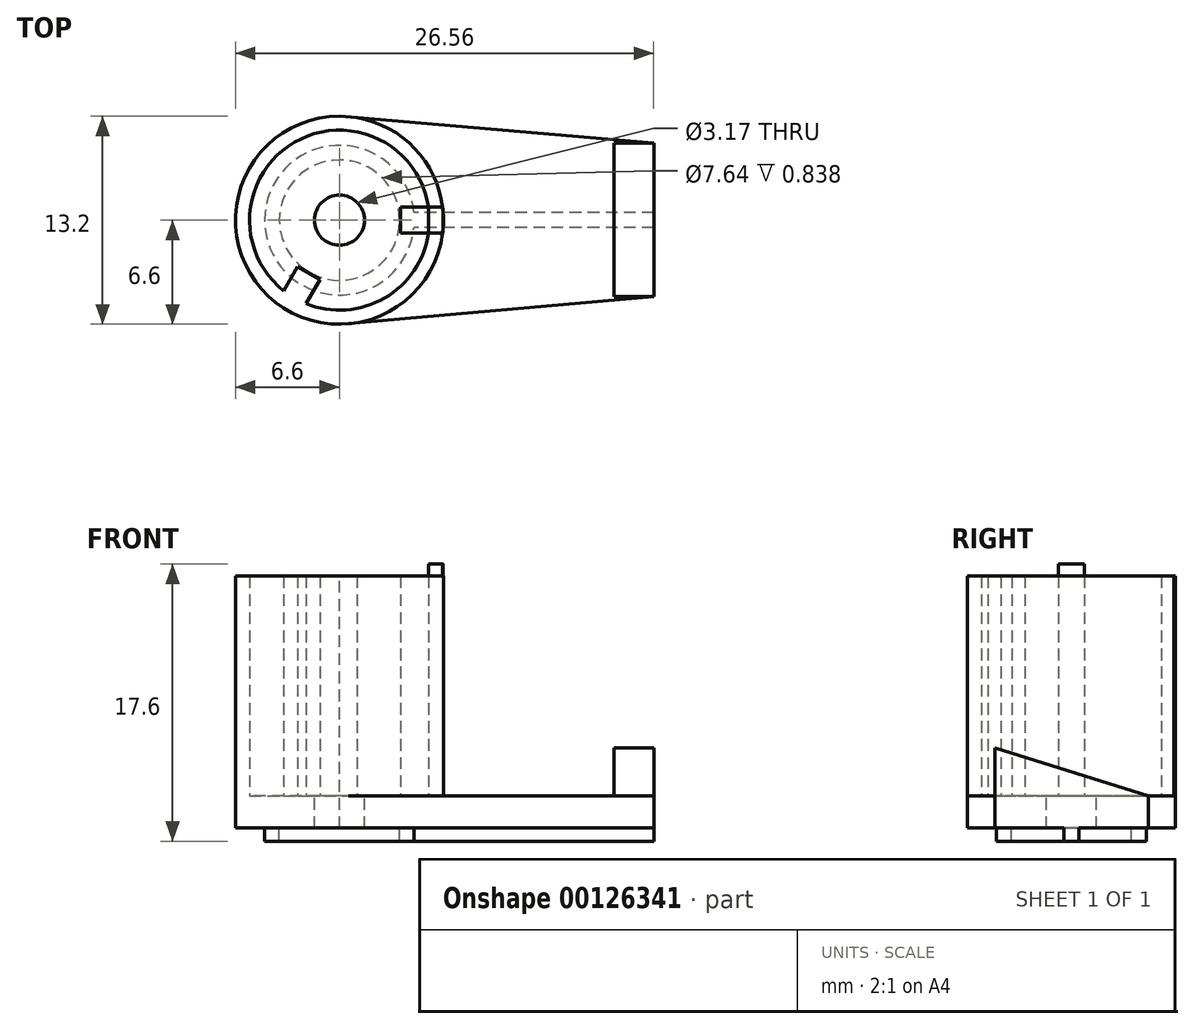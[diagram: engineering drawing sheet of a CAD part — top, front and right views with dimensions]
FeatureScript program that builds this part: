
annotation { "Feature Type Name" : "Feature", "Feature Type Description" : "" }
export const myFeature = defineFeature(function(context is Context, id is Id, definition is map)
    precondition{}
    {
        {
            var Q0;
            Q0=qCreatedBy(makeId("Top.planeOp"),FACE);
            var sketch = newSketch(context, id + "F0", { "sketchPlane" : qUnion([Q0])});
            skCircle(sketch, "E0", {"center": v(0, 0) * mm, "radius": 6.6 * mm});
            skCircle(sketch, "E1.0", {"center": v(0, 0) * mm, "radius": 5.72 * mm});
            skLineSegment(sketch, "E2.right", {"start": v(19.96, 4.9) * mm, "end": v(19.96, -4.85) * mm});
            skLineSegment(sketch, "E3.trimOffspring", {"start": v(0, -6.6) * mm, "end": v(0, -6.7) * mm});
            skLineSegment(sketch, "E4.trimOffspring", {"start": v(0, -6.6) * mm, "end": v(0, -6.63) * mm});
            skLineSegment(sketch, "E5", {"start": v(0, 6.6) * mm, "end": v(19.96, 4.9) * mm});
            skLineSegment(sketch, "E6", {"start": v(0, -6.63) * mm, "end": v(19.96, -4.85) * mm});
            skPoint(sketch, "E7.orphan", {"position": v(19.96, 6.67) * mm});
            skPoint(sketch, "E2.top.end.orphan", {"position": v(19.96, -6.63) * mm});
            skPoint(sketch, "E8.top.end.orphan", {"position": v(-6.7, -6.63) * mm});
            skCircle(sketch, "E9", {"center": v(0, 0) * mm, "radius": 1.59 * mm});
            skSolve(sketch);
        }
        {
            var Q0;
            {var subQ0=sQuery(id+"F0.wireOp",EDGE,"E5");var subQ1=sQuery(id+"F0.wireOp",EDGE,"E0");var subQ2=makeQuery(id+"F0.imprint","INTERSECT",VERTEX,{"disambiguationData":[OD(0.0)],"derivedFrom":[subQ1,subQ0]});Q0=makeQuery(id+"F0.imprint","IMPRINT",FACE,{"disambiguationData":[TD([[makeQuery(id+"F0.imprint","IMPRINT",EDGE,{"disambiguationData":[TD([[subQ2,1.0]])],"derivedFrom":subQ1}),1.0]])]});}
            var Q1;
            {var subQ0=sQuery(id+"F0.wireOp",EDGE,"E4.trimOffspring");Q1=makeQuery(id+"F0.imprint","IMPRINT",FACE,{"disambiguationData":[TD([[makeQuery(id+"F0.imprint","IMPRINT",EDGE,{"derivedFrom":subQ0}),1.0]])]});}
            var Q2;
            Q2=makeQuery(id+"F0.imprint","IMPRINT",FACE,{"disambiguationData":[TD([[makeQuery(id+"F0.imprint","IMPRINT",EDGE,{"derivedFrom":sQuery(id+"F0.wireOp",EDGE,"E1.0")}),-1.0]])]});
            var Q3;
            {var subQ5=sQuery(id+"F0.wireOp",EDGE,"E2.right");Q3=makeQuery(id+"F0.imprint","IMPRINT",FACE,{"disambiguationData":[TD([[makeQuery(id+"F0.imprint","IMPRINT",EDGE,{"derivedFrom":subQ5}),-1.0]])]});}
            var Q4;
            Q4=makeQuery(id+"F0.imprint","IMPRINT",FACE,{"disambiguationData":[TD([[makeQuery(id+"F0.imprint","IMPRINT",EDGE,{"derivedFrom":sQuery(id+"F0.wireOp",EDGE,"E1.0")}),1.0]])]});
            extrude(context, id + "F1", {"entities" : qUnion([Q0, Q1, Q2, Q3, Q4]), "oppositeDirection" : true, "depth" : 2.03 * mm});
        }
        {
            var Q0;
            Q0=makeQuery(id+"F0.imprint","IMPRINT",FACE,{"disambiguationData":[TD([[makeQuery(id+"F0.imprint","IMPRINT",EDGE,{"derivedFrom":sQuery(id+"F0.wireOp",EDGE,"E1.0")}),-1.0]])]});
            extrude(context, id + "F2", {"entities" : qUnion([Q0]), "operationType" : NewBodyOperationType.ADD, "depth" : 13.97 * mm});
        }
        {
            var Q0;
            Q0=makeQuery(id+"F1.opExtrude","SWEPT_FACE",FACE,{"disambiguationData":[OSD([sQuery(id+"F0.wireOp",EDGE,"E2.right")])]});
            var sketch = newSketch(context, id + "F3", { "sketchPlane" : qUnion([Q0])});
            skLineSegment(sketch, "E10", {"start": v(4.9, 0) * mm, "end": v(-4.85, 3.05) * mm});
            skLineSegment(sketch, "E11", {"start": v(-4.85, 3.05) * mm, "end": v(-4.85, 0) * mm});
            skSolve(sketch);
        }
        {
            var Q0;
            Q0 = qSketchRegion(id + "F3", true);
            var Q1;
            Q1=makeQuery(id+"F3.imprint","IMPRINT",FACE,{"disambiguationData":[TD([[makeQuery(id+"F3.imprint","IMPRINT",EDGE,{"derivedFrom":sQuery(id+"F3.wireOp",EDGE,"E10")}),1.0]])]});
            extrude(context, id + "F4", {"entities" : qUnion([Q0, Q1]), "operationType" : NewBodyOperationType.ADD, "oppositeDirection" : true, "depth" : 2.54 * mm});
        }
        {
            var Q0;
            Q0=makeQuery(id+"F0.imprint","IMPRINT",FACE,{"disambiguationData":[TD([[makeQuery(id+"F0.imprint","IMPRINT",EDGE,{"derivedFrom":sQuery(id+"F0.wireOp",EDGE,"E1.0")}),1.0]])]});
            var sketch = newSketch(context, id + "F5", { "sketchPlane" : qUnion([Q0])});
            skLineSegment(sketch, "E12", {"start": v(0, 0) * mm, "end": v(20.41, 0) * mm, "construction": true});
            skLineSegment(sketch, "E13", {"start": v(20.41, 0) * mm, "end": v(5.65, 0) * mm, "construction": true});
            skLineSegment(sketch, "E14.bottom", {"start": v(6.44, -0.82) * mm, "end": v(3.88, -0.82) * mm});
            skLineSegment(sketch, "E14.top", {"start": v(6.44, 0.82) * mm, "end": v(3.88, 0.82) * mm});
            skLineSegment(sketch, "E14.left", {"start": v(6.44, -0.82) * mm, "end": v(6.44, 0.82) * mm});
            skLineSegment(sketch, "E14.right", {"start": v(3.88, -0.82) * mm, "end": v(3.88, 0.82) * mm});
            skPoint(sketch, "E14.middle", {"position": v(5.16, 0) * mm});
            skPoint(sketch, "E15.center", {"position": v(0, 0) * mm});
            skLineSegment(sketch, "E16.1.0", {"start": v(-2.51, -5.98) * mm, "end": v(-1.23, -3.77) * mm});
            skLineSegment(sketch, "E16.1.1", {"start": v(-3.93, -5.17) * mm, "end": v(-2.65, -2.95) * mm});
            skLineSegment(sketch, "E16.1.2", {"start": v(-3.93, -5.17) * mm, "end": v(-2.51, -5.98) * mm});
            skLineSegment(sketch, "E16.1.3", {"start": v(-2.65, -2.95) * mm, "end": v(-1.23, -3.77) * mm});
            skLineSegment(sketch, "E16.anchor1", {"start": v(0, 0) * mm, "end": v(3.88, -0.82) * mm, "construction": true});
            skLineSegment(sketch, "E16.anchor2", {"start": v(0, 0) * mm, "end": v(-2.65, -2.95) * mm, "construction": true});
            skSolve(sketch);
        }
        {
            var Q0;
            Q0 = qSketchRegion(id + "F5", true);
            extrude(context, id + "F6", {"entities" : qUnion([Q0]), "operationType" : NewBodyOperationType.ADD, "depth" : 13.97 * mm});
        }
        {
            var Q0;
            Q0=makeQuery(id+"F1.opExtrude","CAP_FACE",FACE,{"disambiguationData":[OSD([sQuery(id+"F0.wireOp",EDGE,"E0"),sQuery(id+"F0.wireOp",EDGE,"E2.right"),sQuery(id+"F0.wireOp",EDGE,"E4.trimOffspring"),sQuery(id+"F0.wireOp",EDGE,"E5"),sQuery(id+"F0.wireOp",EDGE,"E6"),sQuery(id+"F0.wireOp",EDGE,"E9")])],"isStart":false});
            var sketch = newSketch(context, id + "F7", { "sketchPlane" : qUnion([Q0])});
            skLineSegment(sketch, "E17", {"start": v(0, 0) * mm, "end": v(3.82, 0) * mm, "construction": true});
            skCircle(sketch, "E18", {"center": v(0, 0) * mm, "radius": 3.82 * mm});
            skArc(sketch, "E19.0", {"start": v(4.73, 0.47) * mm, "mid": v(-4.75, 0) * mm, "end": v(4.73, -0.47) * mm});
            skLineSegment(sketch, "E20.bottom", {"start": v(19.96, -0.47) * mm, "end": v(4.73, -0.47) * mm});
            skLineSegment(sketch, "E20.top", {"start": v(19.96, 0.47) * mm, "end": v(4.73, 0.47) * mm});
            skLineSegment(sketch, "E20.left", {"start": v(19.96, -0.47) * mm, "end": v(19.96, 0.47) * mm});
            skPoint(sketch, "E20.middle", {"position": v(11.17, 0) * mm});
            skLineSegment(sketch, "E21.trimOffspring", {"start": v(4.75, 0) * mm, "end": v(19.96, 0) * mm, "construction": true});
            skSolve(sketch);
        }
        {
            var Q0;
            Q0=makeQuery(id+"F7.imprint","IMPRINT",FACE,{"disambiguationData":[TD([[makeQuery(id+"F7.imprint","IMPRINT",EDGE,{"derivedFrom":sQuery(id+"F7.wireOp",EDGE,"E18")}),-1.0]])]});
            extrude(context, id + "F8", {"entities" : qUnion([Q0]), "operationType" : NewBodyOperationType.ADD, "depth" : 0.84 * mm});
        }
        {
            var Q0;
            Q0=makeQuery(id+"F6.boolean.opBoolean","MERGE",FACE,{"derivedFrom":[makeQuery(id+"F2.opExtrude","CAP_FACE",FACE,{"disambiguationData":[OSD([sQuery(id+"F0.wireOp",EDGE,"E0"),sQuery(id+"F0.wireOp",EDGE,"E1.0"),sQuery(id+"F0.wireOp",EDGE,"E5")])],"isStart":false}),makeQuery(id+"F6.opExtrude","CAP_FACE",FACE,{"disambiguationData":[OSD([sQuery(id+"F5.wireOp",EDGE,"E14.bottom"),sQuery(id+"F5.wireOp",EDGE,"E14.top"),sQuery(id+"F5.wireOp",EDGE,"E14.left"),sQuery(id+"F5.wireOp",EDGE,"E14.right")])],"isStart":false}),makeQuery(id+"F6.opExtrude","CAP_FACE",FACE,{"disambiguationData":[OSD([sQuery(id+"F5.wireOp",EDGE,"E16.1.0"),sQuery(id+"F5.wireOp",EDGE,"E16.1.1"),sQuery(id+"F5.wireOp",EDGE,"E16.1.2"),sQuery(id+"F5.wireOp",EDGE,"E16.1.3")])],"isStart":false})]});
            var sketch = newSketch(context, id + "F9", { "sketchPlane" : qUnion([Q0])});
            skLineSegment(sketch, "E22.bottom", {"start": v(5.66, 0.82) * mm, "end": v(6.55, 0.82) * mm});
            skLineSegment(sketch, "E22.top", {"start": v(5.66, -0.82) * mm, "end": v(6.55, -0.82) * mm});
            skLineSegment(sketch, "E22.left", {"start": v(5.66, 0.82) * mm, "end": v(5.66, -0.82) * mm});
            skFitSpline(sketch, "E23", {"points": [v(6.55, 0.82) * mm, v(6.55, -0.82) * mm], "startDerivative": vector(0.15, -2.3) * mm, "endDerivative": vector(-0.15, -2.36) * mm});
            skSolve(sketch);
        }
        {
            var Q0;
            Q0=qCreatedBy(makeId("Front.planeOp"),FACE);
            var sketch = newSketch(context, id + "F10", { "sketchPlane" : qUnion([Q0])});
            skLineSegment(sketch, "E24", {"start": v(0, 0) * mm, "end": v(0, 19.39) * mm, "construction": true});
            skSolve(sketch);
        }
        {
            var Q0;
            {var subQ4=sQuery(id+"F9.wireOp",EDGE,"E22.bottom");Q0=makeQuery(id+"F9.imprint","IMPRINT",FACE,{"disambiguationData":[TD([[makeQuery(id+"F9.imprint","IMPRINT",EDGE,{"derivedFrom":subQ4}),-1.0]])]});}
            extrude(context, id + "F11", {"entities" : qUnion([Q0]), "operationType" : NewBodyOperationType.ADD, "depth" : 0.76 * mm});
        }
    });
